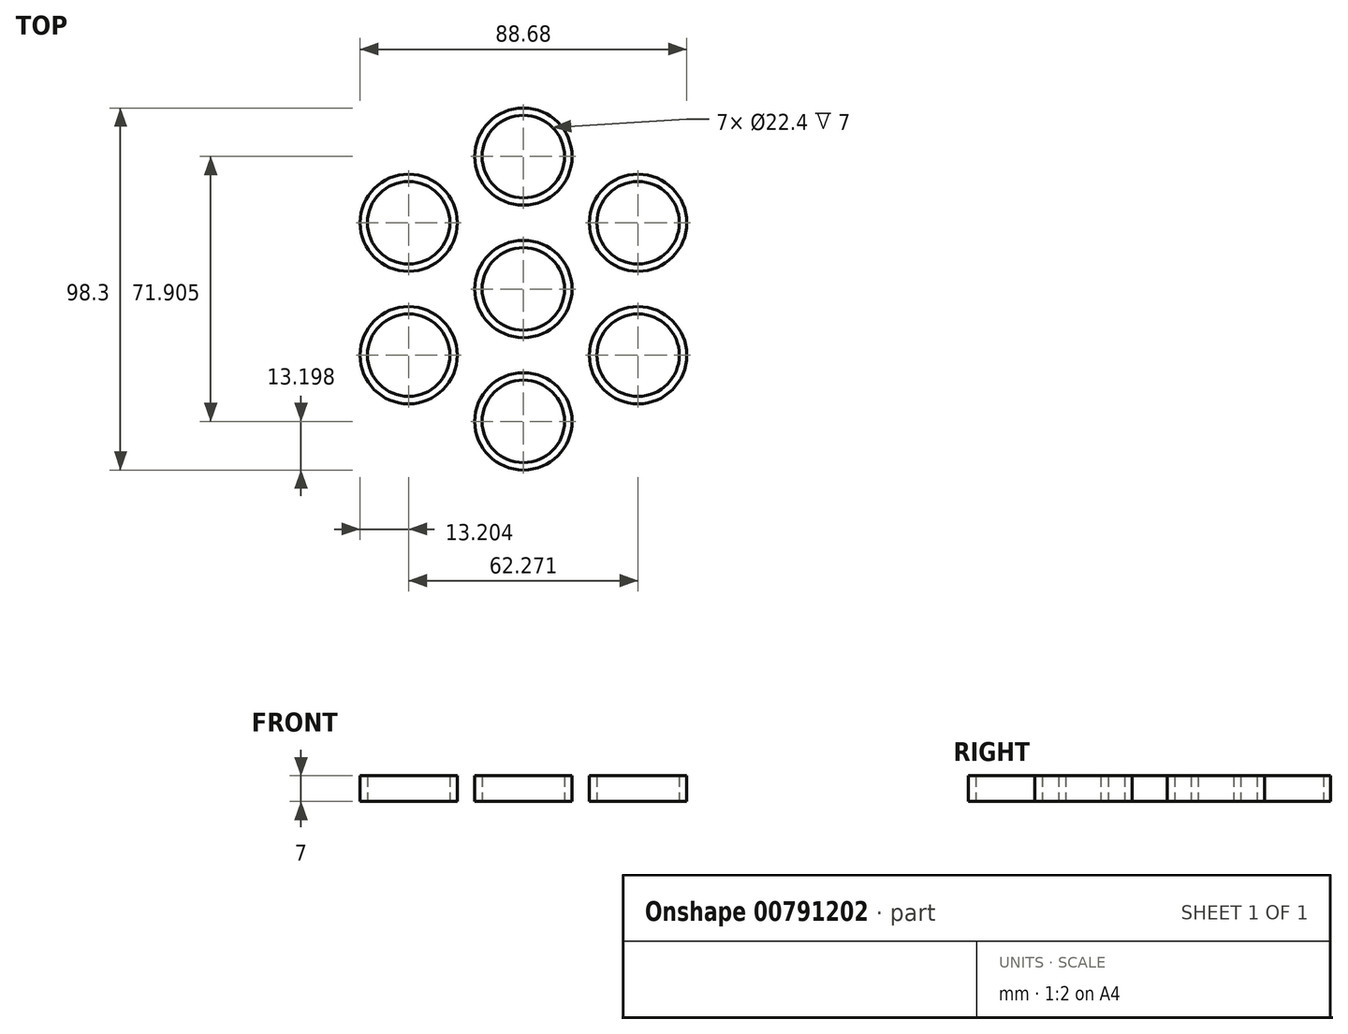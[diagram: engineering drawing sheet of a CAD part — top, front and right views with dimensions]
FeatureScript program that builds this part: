
annotation { "Feature Type Name" : "Feature", "Feature Type Description" : "" }
export const myFeature = defineFeature(function(context is Context, id is Id, definition is map)
    precondition{}
    {
        {
            var Q0;
            Q0=qCreatedBy(makeId("Top.planeOp"),FACE);
            var sketch = newSketch(context, id + "F0", { "sketchPlane" : qUnion([Q0])});
            skCircle(sketch, "E0", {"center": v(0, 0) * mm, "radius": 11.2 * mm});
            skCircle(sketch, "E1", {"center": v(0, 35.95) * mm, "radius": 11.2 * mm});
            skCircle(sketch, "E2", {"center": v(0, 0) * mm, "radius": 13.2 * mm});
            skCircle(sketch, "E3", {"center": v(0, 35.95) * mm, "radius": 13.2 * mm});
            skCircle(sketch, "E4.1.0", {"center": v(-31.14, 17.98) * mm, "radius": 13.2 * mm});
            skCircle(sketch, "E4.1.1", {"center": v(-31.14, 17.98) * mm, "radius": 11.2 * mm});
            skCircle(sketch, "E4.2.0", {"center": v(-31.14, -17.98) * mm, "radius": 13.2 * mm});
            skCircle(sketch, "E4.2.1", {"center": v(-31.14, -17.98) * mm, "radius": 11.2 * mm});
            skCircle(sketch, "E4.3.0", {"center": v(0, -35.95) * mm, "radius": 13.2 * mm});
            skCircle(sketch, "E4.3.1", {"center": v(0, -35.95) * mm, "radius": 11.2 * mm});
            skCircle(sketch, "E4.4.0", {"center": v(31.14, -17.98) * mm, "radius": 13.2 * mm});
            skCircle(sketch, "E4.4.1", {"center": v(31.14, -17.98) * mm, "radius": 11.2 * mm});
            skCircle(sketch, "E4.5.0", {"center": v(31.14, 17.98) * mm, "radius": 13.2 * mm});
            skCircle(sketch, "E4.5.1", {"center": v(31.14, 17.98) * mm, "radius": 11.2 * mm});
            skLineSegment(sketch, "E5", {"start": v(-21.63, 8.82) * mm, "end": v(-12.57, 4.04) * mm});
            skLineSegment(sketch, "E6.1.0", {"start": v(-22.15, -8.3) * mm, "end": v(-13.9, -2.48) * mm});
            skLineSegment(sketch, "E6.1.1", {"start": v(-18.45, -14.33) * mm, "end": v(-9.78, -8.87) * mm});
            skLineSegment(sketch, "E6.2.0", {"start": v(-3.89, -23.34) * mm, "end": v(-4.8, -13.28) * mm});
            skLineSegment(sketch, "E6.2.1", {"start": v(3.18, -23.14) * mm, "end": v(2.79, -12.9) * mm});
            skLineSegment(sketch, "E6.3.0", {"start": v(18.27, -15.03) * mm, "end": v(9.1, -10.8) * mm});
            skLineSegment(sketch, "E6.3.1", {"start": v(21.63, -8.82) * mm, "end": v(12.57, -4.04) * mm});
            skLineSegment(sketch, "E6.4.0", {"start": v(22.15, 8.3) * mm, "end": v(13.9, 2.48) * mm});
            skLineSegment(sketch, "E6.4.1", {"start": v(18.45, 14.33) * mm, "end": v(9.78, 8.87) * mm});
            skLineSegment(sketch, "E6.5.1", {"start": v(-3.18, 23.14) * mm, "end": v(-2.79, 12.9) * mm});
            skSolve(sketch);
        }
        {
            var Q0;
            Q0=makeQuery(id+"F0.imprint","IMPRINT",FACE,{"disambiguationData":[TD([[makeQuery(id+"F0.imprint","IMPRINT",EDGE,{"derivedFrom":sQuery(id+"F0.wireOp",EDGE,"E1")}),-1.0]])]});
            var Q1;
            Q1=makeQuery(id+"F0.imprint","IMPRINT",FACE,{"disambiguationData":[TD([[makeQuery(id+"F0.imprint","IMPRINT",EDGE,{"derivedFrom":sQuery(id+"F0.wireOp",EDGE,"E4.1.1")}),-1.0]])]});
            var Q2;
            Q2=makeQuery(id+"F0.imprint","IMPRINT",FACE,{"disambiguationData":[TD([[makeQuery(id+"F0.imprint","IMPRINT",EDGE,{"derivedFrom":sQuery(id+"F0.wireOp",EDGE,"E4.2.1")}),-1.0]])]});
            var Q3;
            Q3=makeQuery(id+"F0.imprint","IMPRINT",FACE,{"disambiguationData":[TD([[makeQuery(id+"F0.imprint","IMPRINT",EDGE,{"derivedFrom":sQuery(id+"F0.wireOp",EDGE,"E0")}),-1.0]])]});
            var Q4;
            Q4=makeQuery(id+"F0.imprint","IMPRINT",FACE,{"disambiguationData":[TD([[makeQuery(id+"F0.imprint","IMPRINT",EDGE,{"derivedFrom":sQuery(id+"F0.wireOp",EDGE,"E4.5.1")}),-1.0]])]});
            var Q5;
            Q5=makeQuery(id+"F0.imprint","IMPRINT",FACE,{"disambiguationData":[TD([[makeQuery(id+"F0.imprint","IMPRINT",EDGE,{"derivedFrom":sQuery(id+"F0.wireOp",EDGE,"E4.4.1")}),-1.0]])]});
            var Q6;
            Q6=makeQuery(id+"F0.imprint","IMPRINT",FACE,{"disambiguationData":[TD([[makeQuery(id+"F0.imprint","IMPRINT",EDGE,{"derivedFrom":sQuery(id+"F0.wireOp",EDGE,"E4.3.1")}),-1.0]])]});
            extrude(context, id + "F1", {"entities" : qUnion([Q0, Q1, Q2, Q3, Q4, Q5, Q6]), "depth" : 7 * mm, "offsetDistance" : 25 * mm});
        }
    });
